# Revit family: Kendrik
name_source: partatom
category: Furniture
revit_build: Autodesk Revit 2016 (Build: 20160126_1600(x64)
units: mm (PartAtom-declared; Revit-internal decimal feet)

## family parameters
Always vertical = Yes
Cut with Voids When Loaded = No
OmniClass Number = 23.40.20.00
OmniClass Title = General Furniture and Specialties
Room Calculation Point = No
Shared = No
Work Plane-Based = No

## types (9) — shared parameters
Cushion Width = 25"
Depth = 35"
Seat Depth = 24"

## per-type parameters (varying)
| type | Cushion 2 | Cushion 3 | Left Arm | Left Foot Displacement | Non-Corner Unit Geometry | Right Arm | Right Foot Displacement | Seat Width |
| Single Seat (armless) | No | No | No | 13 1/2" | Yes | No | 7 1/2" | 25" |
| Sofa | Yes | Yes | Yes | 8 1/2" | Yes | Yes | 2 1/2" | 75" |
| Loveseat | Yes | No | Yes | 8 1/2" | Yes | Yes | 2 1/2" | 50" |
| Chair | No | No | Yes | 8 1/2" | Yes | Yes | 2 1/2" | 25" |
| Triple Seat (armless) | Yes | Yes | No | 13 1/2" | Yes | No | 7 1/2" | 75" |
| Single Seat Left Arm | No | No | Yes | 8 1/2" | Yes | No | 7 1/2" | 25" |
| Single Seat Right Arm | No | No | No | 13 1/2" | Yes | Yes | 2 1/2" | 25" |
| Corner Unit | No | No | No | 2 1/2" | No | No | 7 1/2" | 25" |
| Double Seat (armless) | Yes | No | No | 13 1/2" | Yes | No | 7 1/2" | 50" |

type visibility flags (boolean, named after types; folded from table):
- Single Seat (armless): Yes: (none)
- Sofa: Yes: (none)
- Loveseat: Yes: (none)
- Chair: Yes: (none)
- Triple Seat (armless): Yes: (none)
- Single Seat Left Arm: Yes: (none)
- Single Seat Right Arm: Yes: (none)
- Corner Unit: Yes: Corner Unit
- Double Seat (armless): Yes: (none)

## geometry (parser evidence)
native form markers: Blend x8, Sweep x23
no freeform markers — native parametric forms only
